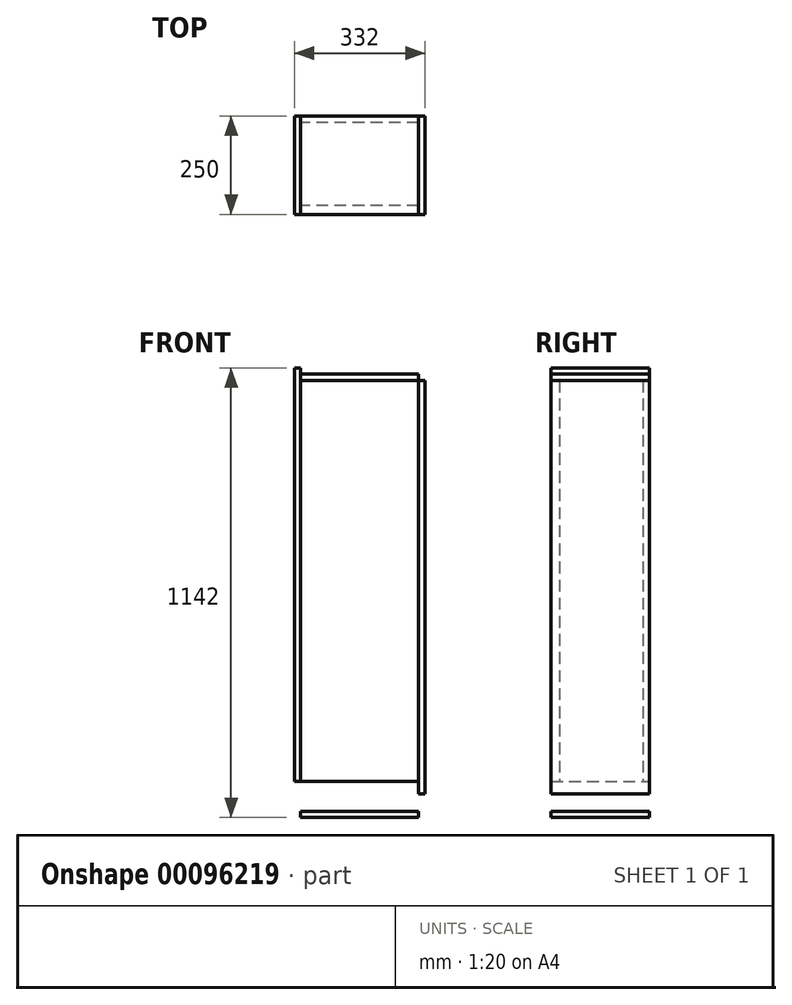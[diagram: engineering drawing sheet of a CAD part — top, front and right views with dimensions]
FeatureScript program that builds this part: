
annotation { "Feature Type Name" : "Feature", "Feature Type Description" : "" }
export const myFeature = defineFeature(function(context is Context, id is Id, definition is map)
    precondition{}
    {
        {
            var Q0;
            Q0=qCreatedBy(makeId("Front.planeOp"),FACE);
            var sketch = newSketch(context, id + "F0", { "sketchPlane" : qUnion([Q0])});
            skLineSegment(sketch, "E0.bottom", {"start": v(150, 509) * mm, "end": v(-150, 509) * mm});
            skLineSegment(sketch, "E0.top", {"start": v(150, -509) * mm, "end": v(-150, -509) * mm});
            skLineSegment(sketch, "E0.left", {"start": v(150, 509) * mm, "end": v(150, -509) * mm});
            skLineSegment(sketch, "E0.right", {"start": v(-150, 509) * mm, "end": v(-150, -509) * mm});
            skPoint(sketch, "E0.middle", {"position": v(0, 0) * mm});
            skSolve(sketch);
        }
        {
            var Q0;
            Q0 = qSketchRegion(id + "F0", true);
            extrude(context, id + "F1", {"entities" : qUnion([Q0]), "depth" : 22 * mm});
        }
        {
            var Q0;
            Q0=makeQuery(id+"F1.opExtrude","SWEPT_FACE",FACE,{"disambiguationData":[OSD([sQuery(id+"F0.wireOp",EDGE,"E0.left")])]});
            var sketch = newSketch(context, id + "F2", { "sketchPlane" : qUnion([Q0])});
            skSolve(sketch);
        }
        {
            var Q0;
            {var subQ0=sQuery(id+"F0.wireOp",EDGE,"E0.left");Q0=makeQuery(id+"F2.imprint","IMPRINT",FACE,{"disambiguationData":[TD([[makeQuery(id+"F2.imprint","IMPRINT",EDGE,{"derivedFrom":makeQuery(id+"F1.opExtrude","CAP_EDGE",EDGE,{"disambiguationData":[OSD([subQ0])],"isStart":true})}),-1.0]])]});}
            cPlane(context, id + "F3", {"entities" : qUnion([Q0]), "cplaneType" : CPlaneType.OFFSET, "offset" : 0 * mm, "width" : 150 * mm, "height" : 150 * mm});
        }
        {
            var Q0;
            Q0=qCreatedBy(id+"F3.planeOp",FACE);
            var sketch = newSketch(context, id + "F4", { "sketchPlane" : qUnion([Q0])});
            skLineSegment(sketch, "E1.0", {"start": v(-22, 509) * mm, "end": v(0, 509) * mm});
            skLineSegment(sketch, "E2.bottom", {"start": v(-22, 509) * mm, "end": v(228, 509) * mm});
            skLineSegment(sketch, "E2.top", {"start": v(-22, -541) * mm, "end": v(228, -541) * mm});
            skLineSegment(sketch, "E2.left", {"start": v(-22, 509) * mm, "end": v(-22, -541) * mm});
            skLineSegment(sketch, "E2.right", {"start": v(228, 509) * mm, "end": v(228, -541) * mm});
            skSolve(sketch);
        }
        {
            var Q0;
            Q0 = qSketchRegion(id + "F4", true);
            extrude(context, id + "F5", {"entities" : qUnion([Q0]), "depth" : 16 * mm});
        }
        {
            var Q0;
            Q0=makeQuery(id+"F1.opExtrude","SWEPT_FACE",FACE,{"disambiguationData":[OSD([sQuery(id+"F0.wireOp",EDGE,"E0.right")])]});
            cPlane(context, id + "F6", {"entities" : qUnion([Q0]), "cplaneType" : CPlaneType.OFFSET, "offset" : 0 * mm, "width" : 150 * mm, "height" : 150 * mm});
        }
        {
            var Q0;
            Q0=qCreatedBy(id+"F6.planeOp",FACE);
            var sketch = newSketch(context, id + "F7", { "sketchPlane" : qUnion([Q0])});
            skLineSegment(sketch, "E3.bottom", {"start": v(22, 541) * mm, "end": v(-228, 541) * mm});
            skLineSegment(sketch, "E3.top", {"start": v(22, -509) * mm, "end": v(-228, -509) * mm});
            skLineSegment(sketch, "E3.left", {"start": v(22, 541) * mm, "end": v(22, -509) * mm});
            skLineSegment(sketch, "E3.right", {"start": v(-228, 541) * mm, "end": v(-228, -509) * mm});
            skSolve(sketch);
        }
        {
            var Q0;
            Q0 = qSketchRegion(id + "F7", true);
            extrude(context, id + "F8", {"entities" : qUnion([Q0]), "depth" : 16 * mm});
        }
        {
            var Q0;
            Q0=makeQuery(id+"F8.opExtrude","SWEPT_FACE",FACE,{"disambiguationData":[OSD([sQuery(id+"F7.wireOp",EDGE,"E3.right")])]});
            cPlane(context, id + "F9", {"entities" : qUnion([Q0]), "cplaneType" : CPlaneType.OFFSET, "offset" : 0 * mm, "width" : 150 * mm, "height" : 150 * mm});
        }
        {
            var Q0;
            Q0=qCreatedBy(id+"F9.planeOp",FACE);
            var sketch = newSketch(context, id + "F10", { "sketchPlane" : qUnion([Q0])});
            skLineSegment(sketch, "E4.0", {"start": v(150, 509) * mm, "end": v(150, -509) * mm});
            skLineSegment(sketch, "E5.0", {"start": v(-150, 509) * mm, "end": v(150, 509) * mm});
            skLineSegment(sketch, "E5.1", {"start": v(-150, 509) * mm, "end": v(-150, -509) * mm});
            skLineSegment(sketch, "E5.2", {"start": v(-150, -509) * mm, "end": v(150, -509) * mm});
            skSolve(sketch);
        }
        {
            var Q0;
            Q0 = qSketchRegion(id + "F10", true);
            extrude(context, id + "F11", {"entities" : qUnion([Q0]), "oppositeDirection" : true, "depth" : 16 * mm});
        }
        {
            var Q0;
            Q0=makeQuery(id+"F11.opExtrude","SWEPT_FACE",FACE,{"disambiguationData":[OSD([sQuery(id+"F10.wireOp",EDGE,"E5.0")])]});
            cPlane(context, id + "F12", {"entities" : qUnion([Q0]), "cplaneType" : CPlaneType.OFFSET, "offset" : 0 * mm, "width" : 150 * mm, "height" : 150 * mm});
        }
        {
            var Q0;
            Q0=qCreatedBy(id+"F12.planeOp",FACE);
            var sketch = newSketch(context, id + "F13", { "sketchPlane" : qUnion([Q0])});
            skLineSegment(sketch, "E6.0", {"start": v(-150, -22) * mm, "end": v(-150, 228) * mm});
            skLineSegment(sketch, "E6.1", {"start": v(150, -22) * mm, "end": v(-150, -22) * mm});
            skLineSegment(sketch, "E6.2", {"start": v(150, -22) * mm, "end": v(150, 228) * mm});
            skLineSegment(sketch, "E6.3", {"start": v(150, 228) * mm, "end": v(-150, 228) * mm});
            skSolve(sketch);
        }
        {
            var Q0;
            Q0 = qSketchRegion(id + "F13", true);
            extrude(context, id + "F14", {"entities" : qUnion([Q0]), "depth" : 16 * mm});
        }
        {
            var Q0;
            Q0=makeQuery(id+"F14.opExtrude","SWEPT_BODY",BODY,{"disambiguationData":[OSD([sQuery(id+"F13.wireOp",EDGE,"E6.0"),sQuery(id+"F13.wireOp",EDGE,"E6.1"),sQuery(id+"F13.wireOp",EDGE,"E6.2"),sQuery(id+"F13.wireOp",EDGE,"E6.3")])]});
            transform(context, id + "F15", {"entities" : qUnion([Q0]), "transformType" : TransformType.TRANSLATION_3D, "dx" : 0 * mm, "dy" : 0 * mm, "dz" : -1110 * mm, "makeCopy" : true});
        }
    });
